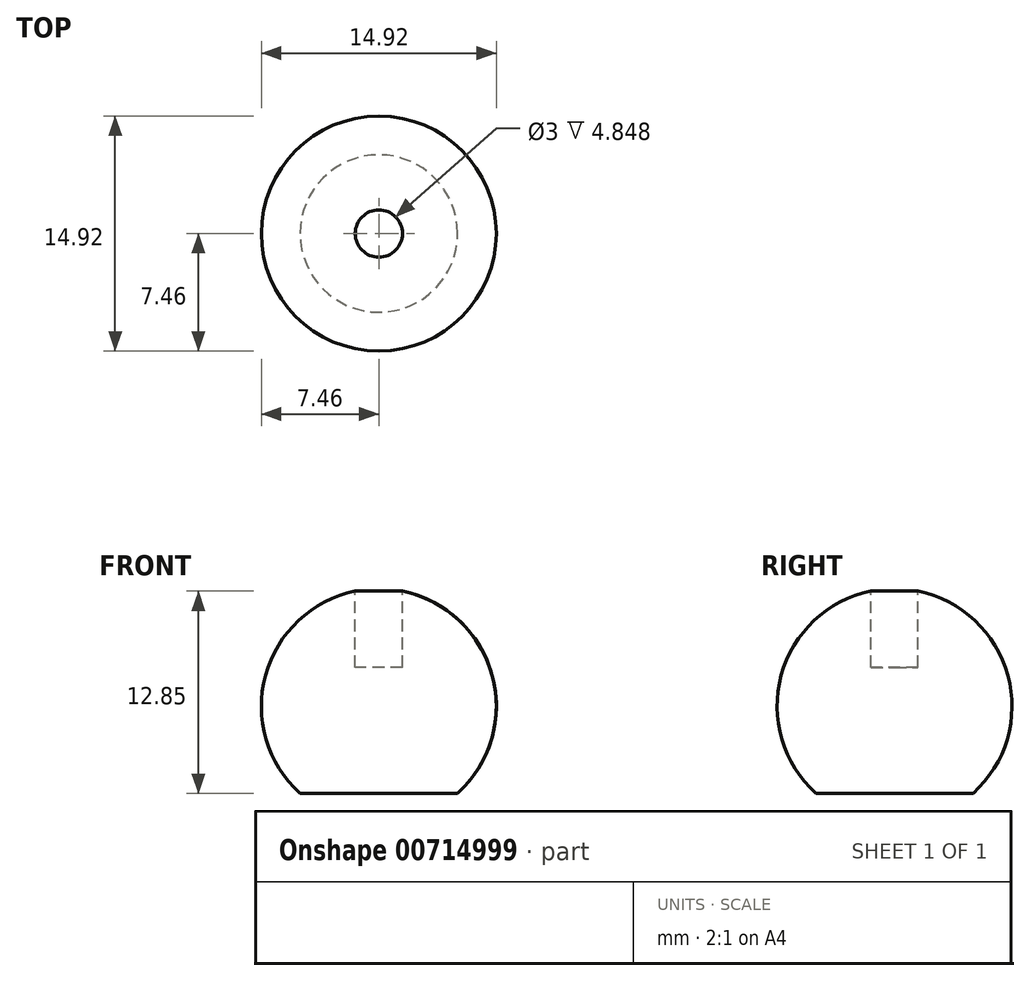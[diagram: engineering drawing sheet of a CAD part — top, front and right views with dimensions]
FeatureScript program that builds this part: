
annotation { "Feature Type Name" : "Feature", "Feature Type Description" : "" }
export const myFeature = defineFeature(function(context is Context, id is Id, definition is map)
    precondition{}
    {
        {
            var Q0;
            Q0=qCreatedBy(makeId("Front.planeOp"),FACE);
            var sketch = newSketch(context, id + "F0", { "sketchPlane" : qUnion([Q0])});
            skLineSegment(sketch, "E0.bottom", {"start": v(0, 0) * mm, "end": v(7.5, 0) * mm, "construction": true});
            skLineSegment(sketch, "E0.top", {"start": v(1.5, 13) * mm, "end": v(7.5, 13) * mm, "construction": true});
            skLineSegment(sketch, "E0.left", {"start": v(0, 0) * mm, "end": v(0, 8) * mm, "construction": true});
            skLineSegment(sketch, "E0.right", {"start": v(7.5, 0) * mm, "end": v(7.5, 13) * mm, "construction": true});
            skLineSegment(sketch, "E1", {"start": v(0, 0) * mm, "end": v(5, 0) * mm, "construction": true});
            skArc(sketch, "E2", {"start": v(5, 0) * mm, "mid": v(7.2, 7.5) * mm, "end": v(1.5, 12.85) * mm});
            skLineSegment(sketch, "E3", {"start": v(5, 0) * mm, "end": v(0, 0) * mm});
            skLineSegment(sketch, "E4", {"start": v(0, 8) * mm, "end": v(0, 0) * mm});
            skLineSegment(sketch, "E5.top", {"start": v(0, 8) * mm, "end": v(1.5, 8) * mm});
            skLineSegment(sketch, "E5.right", {"start": v(1.5, 12.85) * mm, "end": v(1.5, 8) * mm});
            skPoint(sketch, "E6.orphan", {"position": v(0, 13) * mm});
            skSolve(sketch);
        }
        {
            var Q0;
            Q0=makeQuery(id+"F0.imprint","IMPRINT",FACE,{"disambiguationData":[TD([[makeQuery(id+"F0.imprint","IMPRINT",EDGE,{"derivedFrom":sQuery(id+"F0.wireOp",EDGE,"E2")}),1.0]])]});
            var Q1;
            Q1=sQuery(id+"F0.wireOp",EDGE,"E4");
            revolve(context, id + "F1", {"surfaceOperationType" : NewSurfaceOperationType.NEW, "entities" : qUnion([Q0]), "axis" : qUnion([Q1]), "revolveType" : RevolveType.FULL});
        }
    });
